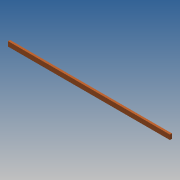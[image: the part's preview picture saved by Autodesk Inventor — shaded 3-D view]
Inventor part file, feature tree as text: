
AUTODESK INVENTOR PART (.ipt)
format: ipt  version: 2013 (Build 170138000, 138)  size: 69,120 bytes
history: native  units: in
note: dims shown in document units (in); Inventor stores cm internally (conversion verified against a paired STEP export)
features: extrude x1, sketch x1
ambient origin geometry x8: Origin, YZ Plane, XZ Plane, XY Plane, X Axis, Y Axis, Z Axis, Center Point
bodies: Solid1 (feature_tree)
feature tree (2):
  extrude  "Extrusion1"  Depth=3.5in
  sketch  "Sketch1"  dims[d0=1.5in d1=3.5in d2=120.0in d3=0.0in]
